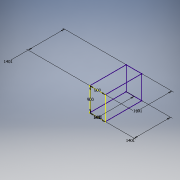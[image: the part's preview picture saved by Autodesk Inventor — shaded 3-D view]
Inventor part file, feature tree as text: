
AUTODESK INVENTOR PART (.ipt)
format: ipt  version: 2016 (Build 200138000, 138)  size: 93,696 bytes
history: native  units: mm
features: sketch x2
ambient origin geometry x8: Origin, YZ Plane, XZ Plane, XY Plane, X Axis, Y Axis, Z Axis, Center Point
feature tree (2):
  sketch  "Boceto1"  dims[d1=600.0mm]
  sketch  "Boceto 3D2"  dims[d2=900.0mm d3=600.0mm d4=1401.0mm d5=1401.0mm d6=1401.0mm d7=1401.0mm]
